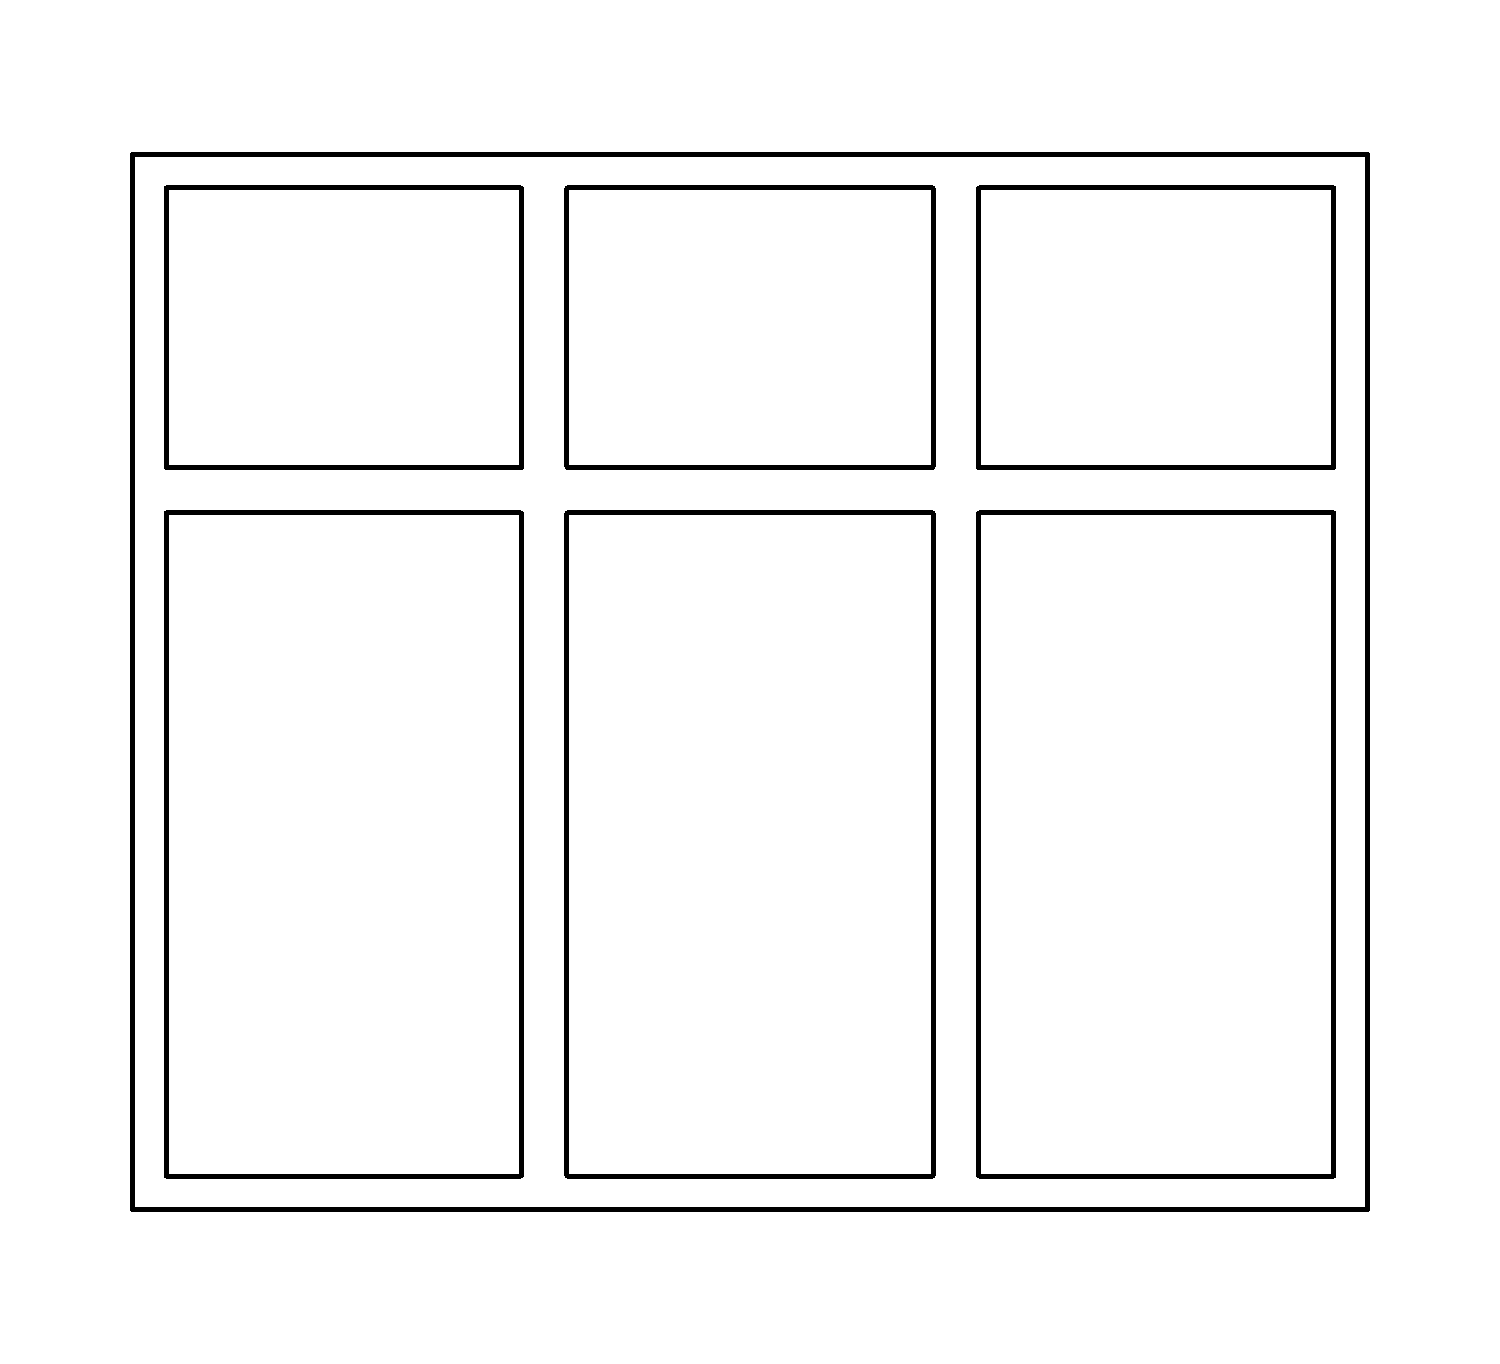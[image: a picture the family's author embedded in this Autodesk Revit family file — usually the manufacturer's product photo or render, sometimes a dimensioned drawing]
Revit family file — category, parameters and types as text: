
# Revit family: окна.rehau_трехпольное_3_фрамуги_сверху
name_source: partatom
category: Окна
revit_build: Autodesk Revit 2017 (Build: 20171027_0315(x64)
units: mm (PartAtom-declared; Revit-internal decimal feet)

## family parameters
Всегда вертикально = Да
Заголовок OmniClass = Windows
Номер OmniClass = 23.30.20.00
Общий = Нет
Основа = Стена
При загрузке вырезать с полостями = Нет
Точка расчета площади = Нет

## types (2) — shared parameters
24_мм = 24мм 1-камерный
32_мм = 32мм 2-камерный
40_мм = 40мм 2-камерный
42_мм = 42мм 2-камерный
50_мм = 50мм 2-камерный
60_blitz_new = 60 BLITZ NEW
60_euro_64 = 60 EURO (коробка 64, импост 78, створка 60)
60_euro_68 = 60 EURO (коробка 68, импост 78, створка 60)
60_euro_76 = 60 EURO (коробка 76, импост 86, створка 74)
70_delight_78 = 70 DELIGHT
70_grazio_55 = 70 GRAZIO (коробка 55)
70_grazio_63 = 70 GRAZIO (коробка 63)
80_intelio_58r = 80 INTELIO (коробка 58, створка R57)
80_intelio_58z = 80 INTELIO (коробка 58, створка Z57)
80_intelio_65r = 80 INTELIO (коробка 65, створка R57)
80_intelio_65z = 80 INTELIO (коробка 65, створка Z57)
ADSK_Обозначение = ГОСТ 30674-99
URL = https://www.rehau.com
sp_energy = Энергосберегающие стекла
sp_gaz = Заполненный газом
sp_standart = Обычный стеклопакет
sp_triplex = Триплекс
Аналитическая конструкция = Окна с одинарным остеклением - для жилых зданий
Высота подоконника по умолчанию = 900 мм
Высота створок снизу = 1200 мм
Группа модели = ОП
Замыкание стены = По основе
Изготовитель = Rehau
Изображение типоразмера = схема_трехпольное_3_фрамуги_сверху.png
Коэффициент теплопередачи (U) = 5.7361 Вт/(м²·K)
Коэффициент теплопритока от солнечного излучения = 0.86
Материал коробки = <По категории>
Материал отлива = <По категории>
Материал подоконника = <По категории>
Материал стекла = <По категории>
Описание = проем.окно
Примерная высота = 1760 мм
Примерная ширина = 2060 мм
Пропускание видимого света = 0.9
Равные створки = Да
Створка слева = 400 мм
Створка справа = 400 мм
Термостойкость = 0.1743 (м²·K)/Вт
Тип верхней створки слева = створка : глухая
Тип верхней створки справа = створка : глухая
Тип верхней створки центр = створка : глухая
Тип нижней створки центр = створка : глухая
глухая_створка = створка : глухая
обозначение_проема_высота = 293 мм
обозначение_проема_ширина = 343 мм
таблица выбора = каталог профилей Rehau

## per-type parameters (varying)
| type | Тип нижней створки слева | Тип нижней створки справа |
| 2060х1760 (2 створки и глухое) | створка : левая-откидная | створка : правая-откидная |
| 2060х1760 (глухое) | створка : глухая | створка : глухая |
